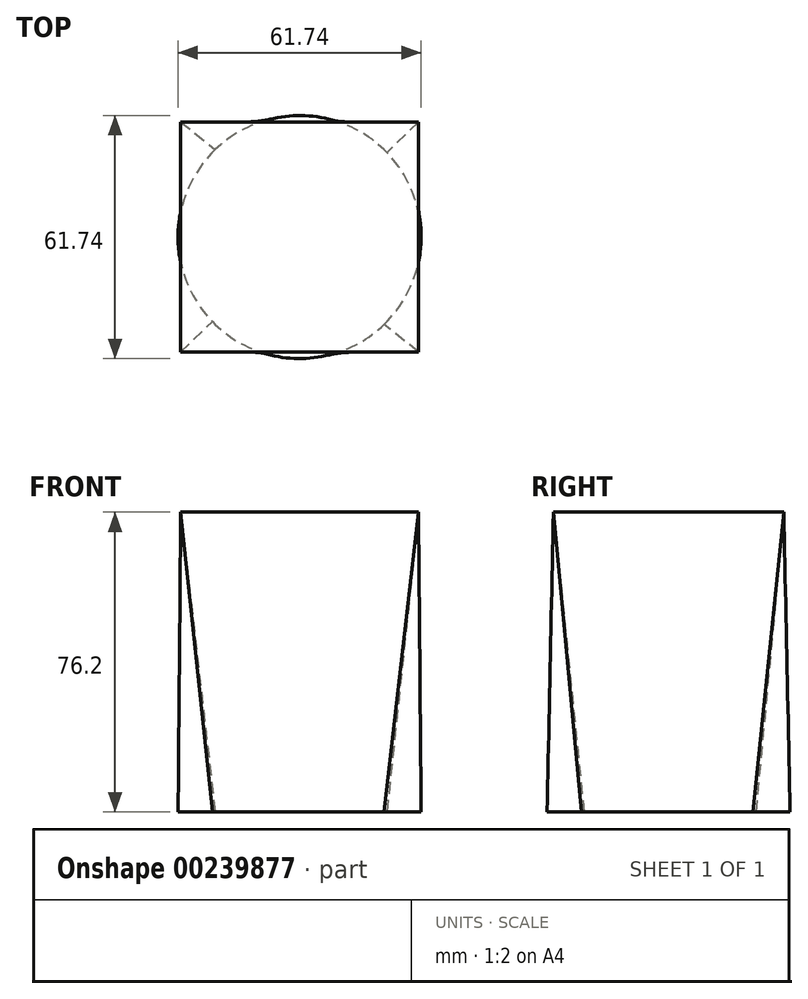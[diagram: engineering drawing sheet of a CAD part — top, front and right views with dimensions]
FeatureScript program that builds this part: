
annotation { "Feature Type Name" : "Feature", "Feature Type Description" : "" }
export const myFeature = defineFeature(function(context is Context, id is Id, definition is map)
    precondition{}
    {
        {
            var Q0;
            Q0=qCreatedBy(makeId("Top.planeOp"),FACE);
            cPlane(context, id + "F0", {"entities" : qUnion([Q0]), "cplaneType" : CPlaneType.OFFSET, "offset" : 76.2 * mm, "width" : 152.4 * mm, "height" : 152.4 * mm});
        }
        {
            var Q0;
            Q0=qCreatedBy(makeId("Top.planeOp"),FACE);
            var sketch = newSketch(context, id + "F1", { "sketchPlane" : qUnion([Q0])});
            skCircle(sketch, "E0", {"center": v(0, 0) * mm, "radius": 30.87 * mm});
            skSolve(sketch);
        }
        {
            var Q0;
            Q0=qCreatedBy(id+"F0.planeOp",FACE);
            var sketch = newSketch(context, id + "F2", { "sketchPlane" : qUnion([Q0])});
            skLineSegment(sketch, "E1.bottom", {"start": v(30.2, 29.27) * mm, "end": v(-30.2, 29.27) * mm});
            skLineSegment(sketch, "E1.top", {"start": v(30.2, -29.27) * mm, "end": v(-30.2, -29.27) * mm});
            skLineSegment(sketch, "E1.left", {"start": v(30.2, 29.27) * mm, "end": v(30.2, -29.27) * mm});
            skLineSegment(sketch, "E1.right", {"start": v(-30.2, 29.27) * mm, "end": v(-30.2, -29.27) * mm});
            skPoint(sketch, "E1.middle", {"position": v(0, 0) * mm});
            skSolve(sketch);
        }
        {
            var Q0;
            Q0=makeQuery(id+"F2.imprint","IMPRINT",FACE,{"disambiguationData":[TD([[makeQuery(id+"F2.imprint","IMPRINT",EDGE,{"derivedFrom":sQuery(id+"F2.wireOp",EDGE,"E1.bottom")}),1.0]])]});
            var Q1;
            Q1=makeQuery(id+"F1.imprint","IMPRINT",FACE,{"disambiguationData":[TD([[makeQuery(id+"F1.imprint","IMPRINT",EDGE,{"derivedFrom":sQuery(id+"F1.wireOp",EDGE,"E0")}),1.0]])]});
            loft(context, id + "F3", {"sheetProfilesArray" : [{ "sheetProfileEntities" : qUnion([Q0]) }, { "sheetProfileEntities" : qUnion([Q1]) }]});
        }
    });
